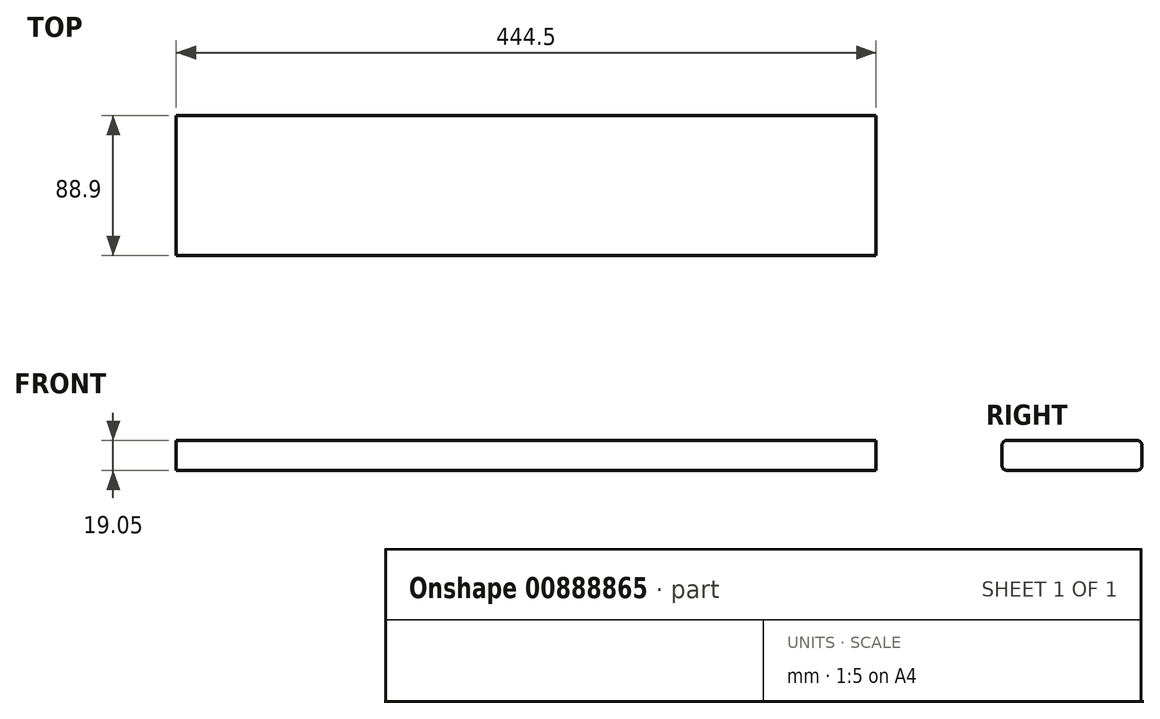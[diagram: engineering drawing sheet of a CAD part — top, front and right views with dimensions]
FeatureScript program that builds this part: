
annotation { "Feature Type Name" : "Feature", "Feature Type Description" : "" }
export const myFeature = defineFeature(function(context is Context, id is Id, definition is map)
    precondition{}
    {
        {
            var Q0;
            Q0=qCreatedBy(makeId("Top.planeOp"),FACE);
            var sketch = newSketch(context, id + "F0", { "sketchPlane" : qUnion([Q0])});
            skLineSegment(sketch, "E0.bottom", {"start": v(222.25, -44.45) * mm, "end": v(-222.25, -44.45) * mm});
            skLineSegment(sketch, "E0.top", {"start": v(222.25, 44.45) * mm, "end": v(-222.25, 44.45) * mm});
            skLineSegment(sketch, "E0.left", {"start": v(222.25, -44.45) * mm, "end": v(222.25, 44.45) * mm});
            skLineSegment(sketch, "E0.right", {"start": v(-222.25, -44.45) * mm, "end": v(-222.25, 44.45) * mm});
            skPoint(sketch, "E0.middle", {"position": v(0, 0) * mm});
            skSolve(sketch);
        }
        {
            var Q0;
            Q0 = qSketchRegion(id + "F0", true);
            extrude(context, id + "F1", {"entities" : qUnion([Q0]), "depth" : 19.05 * mm, "offsetDistance" : 25.4 * mm});
        }
        {
            var Q0;
            Q0=makeQuery(id+"F1.opExtrude","CAP_EDGE",EDGE,{"disambiguationData":[OSD([sQuery(id+"F0.wireOp",EDGE,"E0.top")])],"isStart":false});
            var Q1;
            Q1=makeQuery(id+"F1.opExtrude","CAP_EDGE",EDGE,{"disambiguationData":[OSD([sQuery(id+"F0.wireOp",EDGE,"E0.bottom")])],"isStart":false});
            var Q2;
            Q2=makeQuery(id+"F1.opExtrude","CAP_EDGE",EDGE,{"disambiguationData":[OSD([sQuery(id+"F0.wireOp",EDGE,"E0.top")])],"isStart":true});
            var Q3;
            Q3=makeQuery(id+"F1.opExtrude","CAP_EDGE",EDGE,{"disambiguationData":[OSD([sQuery(id+"F0.wireOp",EDGE,"E0.bottom")])],"isStart":true});
            fillet(context, id + "F2", {"entities" : qUnion([Q0, Q1, Q2, Q3]), "radius" : 3.17 * mm, "tangentPropagation" : true, "allowEdgeOverflow" : false});
        }
    });
